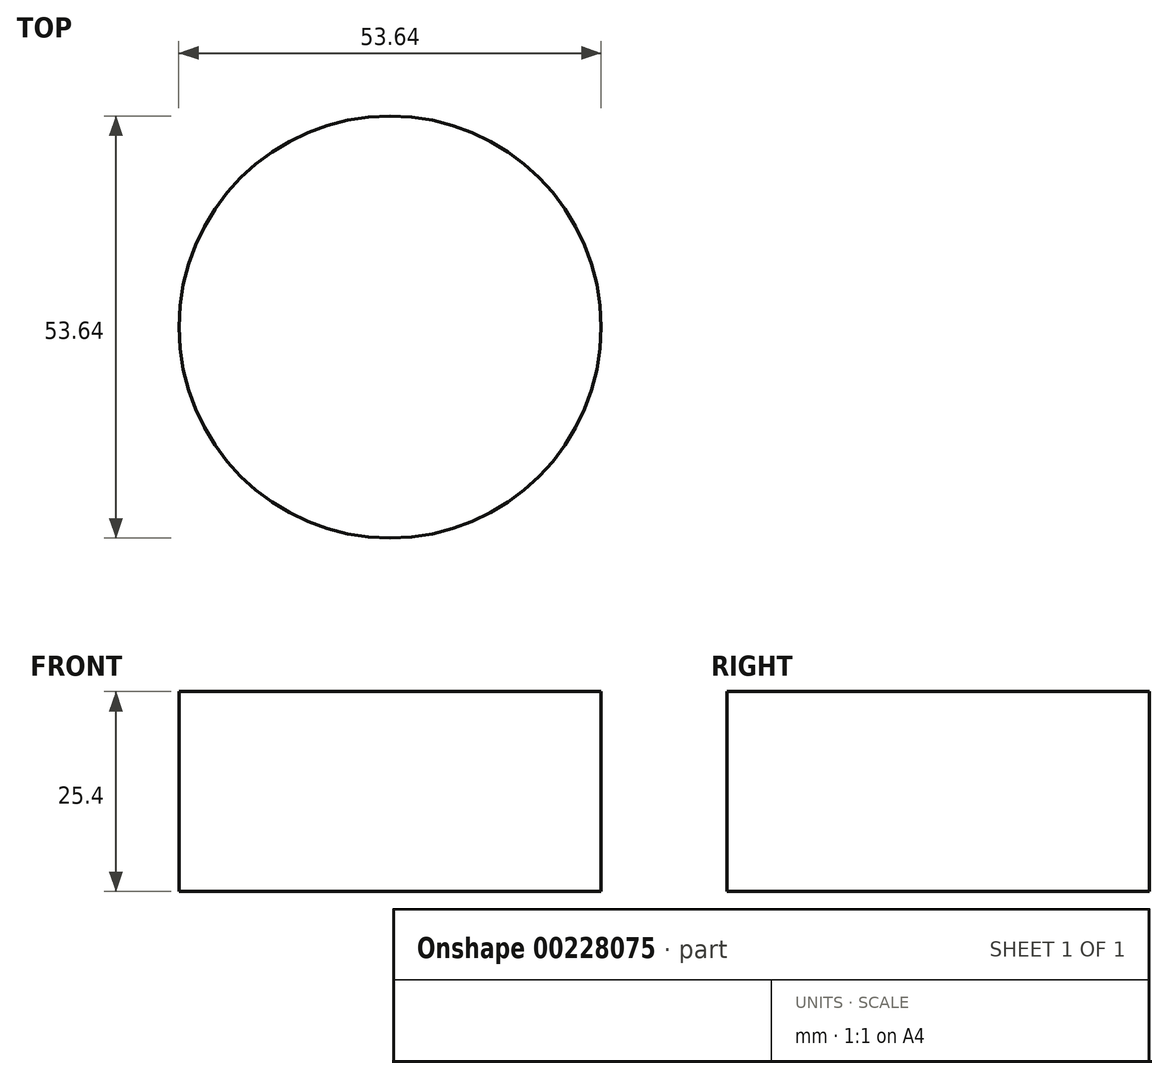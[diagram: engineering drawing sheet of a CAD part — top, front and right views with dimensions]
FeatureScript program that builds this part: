
annotation { "Feature Type Name" : "Feature", "Feature Type Description" : "" }
export const myFeature = defineFeature(function(context is Context, id is Id, definition is map)
    precondition{}
    {
        {
            var Q0;
            Q0=qCreatedBy(makeId("Top.planeOp"),FACE);
            var sketch = newSketch(context, id + "F0", { "sketchPlane" : qUnion([Q0])});
            skCircle(sketch, "E0", {"center": v(0, 0) * mm, "radius": 26.82 * mm});
            skSolve(sketch);
        }
        {
            var Q0;
            Q0=makeQuery(id+"F0.imprint","IMPRINT",FACE,{"disambiguationData":[TD([[makeQuery(id+"F0.imprint","IMPRINT",EDGE,{"derivedFrom":sQuery(id+"F0.wireOp",EDGE,"E0")}),1.0]])]});
            extrude(context, id + "F1", {"entities" : qUnion([Q0]), "depth" : 25.4 * mm});
        }
    });
